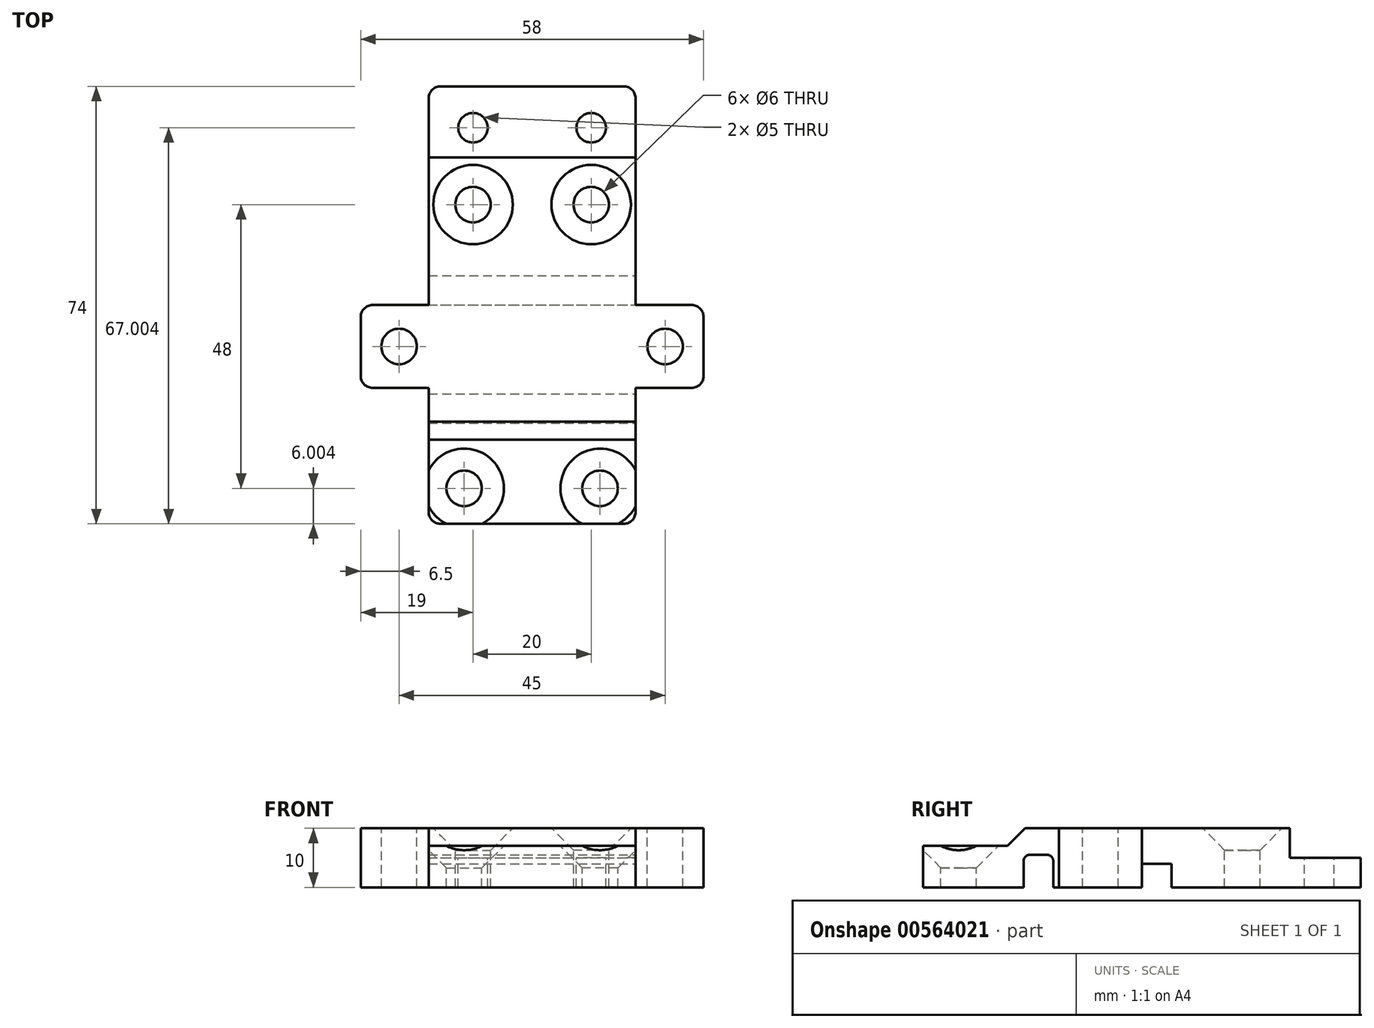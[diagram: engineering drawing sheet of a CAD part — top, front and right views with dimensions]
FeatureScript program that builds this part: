
annotation { "Feature Type Name" : "Feature", "Feature Type Description" : "" }
export const myFeature = defineFeature(function(context is Context, id is Id, definition is map)
    precondition{}
    {
        {
            var Q0;
            Q0=qCreatedBy(makeId("Top.planeOp"),FACE);
            var sketch = newSketch(context, id + "F0", { "sketchPlane" : qUnion([Q0])});
            skLineSegment(sketch, "E0.bottom", {"start": v(0, 48.2) * mm, "end": v(17.5, 48.2) * mm});
            skLineSegment(sketch, "E0.top", {"start": v(0, -25.8) * mm, "end": v(17.5, -25.8) * mm});
            skLineSegment(sketch, "E0.left", {"start": v(0, 48.2) * mm, "end": v(0, -25.8) * mm});
            skLineSegment(sketch, "E0.right", {"start": v(17.5, 48.2) * mm, "end": v(17.5, -25.8) * mm});
            skLineSegment(sketch, "E1.bottom", {"start": v(17.5, -2.8) * mm, "end": v(29, -2.8) * mm});
            skLineSegment(sketch, "E1.top", {"start": v(17.5, 11.2) * mm, "end": v(29, 11.2) * mm});
            skLineSegment(sketch, "E1.left", {"start": v(17.5, -2.8) * mm, "end": v(17.5, 11.2) * mm});
            skLineSegment(sketch, "E1.right", {"start": v(29, -2.8) * mm, "end": v(29, 11.2) * mm});
            skSolve(sketch);
        }
        {
            var Q0;
            Q0=makeQuery(id+"F0.imprint","IMPRINT",FACE,{"disambiguationData":[TD([[makeQuery(id+"F0.imprint","IMPRINT",EDGE,{"derivedFrom":sQuery(id+"F0.wireOp",EDGE,"E1.bottom")}),1.0]])]});
            var Q1;
            {var subQ1=sQuery(id+"F0.wireOp",EDGE,"E0.bottom");Q1=makeQuery(id+"F0.imprint","IMPRINT",FACE,{"disambiguationData":[TD([[makeQuery(id+"F0.imprint","IMPRINT",EDGE,{"derivedFrom":subQ1}),-1.0]])]});}
            extrude(context, id + "F1", {"entities" : qUnion([Q0, Q1]), "depth" : 10 * mm, "offsetDistance" : 25 * mm});
        }
        {
            var Q0;
            {var subQ0=sQuery(id+"F0.wireOp",EDGE,"E0.right");Q0=makeQuery(id+"F1.opExtrude","SWEPT_FACE",FACE,{"disambiguationData":[OSD([subQ0]),TDD([makeQuery(id+"F0.imprint","IMPRINT",EDGE,{"disambiguationData":[TD([[makeQuery(id+"F0.imprint","INTERSECT",VERTEX,{"derivedFrom":[sQuery(id+"F0.wireOp",EDGE,"E0.top"),subQ0]}),1.0]])],"derivedFrom":subQ0})])]});}
            var sketch = newSketch(context, id + "F2", { "sketchPlane" : qUnion([Q0])});
            skLineSegment(sketch, "E2", {"start": v(-25.8, 7) * mm, "end": v(-11.54, 7) * mm});
            skLineSegment(sketch, "E3", {"start": v(-11.54, 7) * mm, "end": v(-8.54, 10) * mm});
            skLineSegment(sketch, "E4", {"start": v(-8.54, 10) * mm, "end": v(-25.8, 10) * mm});
            skLineSegment(sketch, "E5", {"start": v(-25.8, 10) * mm, "end": v(-25.8, 7) * mm});
            skLineSegment(sketch, "E6.bottom", {"start": v(-8.8, 0) * mm, "end": v(-3.8, 0) * mm});
            skLineSegment(sketch, "E6.top", {"start": v(-8.8, 5.5) * mm, "end": v(-3.8, 5.5) * mm});
            skLineSegment(sketch, "E6.left", {"start": v(-8.8, 0) * mm, "end": v(-8.8, 5.5) * mm});
            skLineSegment(sketch, "E6.right", {"start": v(-3.8, 0) * mm, "end": v(-3.8, 5.5) * mm});
            skLineSegment(sketch, "E7", {"start": v(-6.3, 5.5) * mm, "end": v(-6.3, -14.92) * mm, "construction": true});
            skCircle(sketch, "E8", {"center": v(-8.8, 5.5) * mm, "radius": 3 * mm, "construction": true});
            skLineSegment(sketch, "E9.bottom", {"start": v(11.2, 0) * mm, "end": v(16.2, 0) * mm});
            skLineSegment(sketch, "E9.top", {"start": v(11.2, 4) * mm, "end": v(16.2, 4) * mm});
            skLineSegment(sketch, "E9.left", {"start": v(11.2, 0) * mm, "end": v(11.2, 4) * mm});
            skLineSegment(sketch, "E9.right", {"start": v(16.2, 0) * mm, "end": v(16.2, 4) * mm});
            skLineSegment(sketch, "E10.bottom", {"start": v(48.2, 10) * mm, "end": v(36.2, 10) * mm});
            skLineSegment(sketch, "E10.top", {"start": v(48.2, 5) * mm, "end": v(36.2, 5) * mm});
            skLineSegment(sketch, "E10.left", {"start": v(48.2, 10) * mm, "end": v(48.2, 5) * mm});
            skLineSegment(sketch, "E10.right", {"start": v(36.2, 10) * mm, "end": v(36.2, 5) * mm});
            skSolve(sketch);
        }
        {
            var Q0;
            Q0 = qSketchRegion(id + "F2", true);
            extrude(context, id + "F3", {"entities" : qUnion([Q0]), "operationType" : NewBodyOperationType.REMOVE, "endBound" : BoundingType.THROUGH_ALL, "oppositeDirection" : true, "depth" : 25 * mm, "offsetDistance" : 25 * mm});
        }
        {
            var Q0;
            Q0=makeQuery(id+"F3.boolean.opBoolean","COPY",FACE,{"derivedFrom":makeQuery(id+"F3.opExtrude","SWEPT_FACE",FACE,{"disambiguationData":[OSD([sQuery(id+"F2.wireOp",EDGE,"E10.top")])]})});
            var sketch = newSketch(context, id + "F4", { "sketchPlane" : qUnion([Q0])});
            skPoint(sketch, "E11", {"position": v(10, 41.2) * mm});
            skSolve(sketch);
        }
        {
            var Q0;
            Q0=makeQuery(id+"F1.opExtrude","CAP_FACE",FACE,{"disambiguationData":[OSD([sQuery(id+"F0.wireOp",EDGE,"E0.bottom"),sQuery(id+"F0.wireOp",EDGE,"E0.top"),sQuery(id+"F0.wireOp",EDGE,"E0.left"),sQuery(id+"F0.wireOp",EDGE,"E0.right"),sQuery(id+"F0.wireOp",EDGE,"E1.bottom"),sQuery(id+"F0.wireOp",EDGE,"E1.top"),sQuery(id+"F0.wireOp",EDGE,"E1.right")])],"isStart":false});
            var sketch = newSketch(context, id + "F5", { "sketchPlane" : qUnion([Q0])});
            skPoint(sketch, "E12", {"position": v(22.5, 4.2) * mm});
            skLineSegment(sketch, "E13", {"start": v(22.5, 4.2) * mm, "end": v(29, 4.2) * mm, "construction": true});
            skPoint(sketch, "E14", {"position": v(10, 28.2) * mm});
            skSolve(sketch);
        }
        {
            var Q0;
            Q0=makeQuery(id+"F3.boolean.opBoolean","COPY",FACE,{"derivedFrom":makeQuery(id+"F3.opExtrude","SWEPT_FACE",FACE,{"disambiguationData":[OSD([sQuery(id+"F2.wireOp",EDGE,"E2")])]})});
            var sketch = newSketch(context, id + "F6", { "sketchPlane" : qUnion([Q0])});
            skPoint(sketch, "E15", {"position": v(11.5, -19.8) * mm});
            skSolve(sketch);
        }
        {
            var Q0;
            Q0=sQuery(id+"F4.wireOp",VERTEX,"E11");
            var Q1;
            Q1=makeQuery(id+"F1.opExtrude","SWEPT_BODY",BODY,{"disambiguationData":[OSD([sQuery(id+"F0.wireOp",EDGE,"E0.bottom"),sQuery(id+"F0.wireOp",EDGE,"E0.top"),sQuery(id+"F0.wireOp",EDGE,"E0.left"),sQuery(id+"F0.wireOp",EDGE,"E0.right"),sQuery(id+"F0.wireOp",EDGE,"E1.bottom"),sQuery(id+"F0.wireOp",EDGE,"E1.top"),sQuery(id+"F0.wireOp",EDGE,"E1.right")])]});
            hole(context, id + "F7", {"style" : HoleStyle.SIMPLE, "endStyle" : HoleEndStyle.THROUGH, "standardTappedOrClearance" : lookupTablePath({ "standard" : "ISO", "engagement" : "75%", "pitch" : "1 mm", "size" : "M6", "type" : "Tapped" }), "standardBlindInLast" : lookupTablePath({ "standard" : "ISO", "engagement" : "75%", "pitch" : "1 mm", "size" : "M6", "type" : "Tapped" }), "holeDiameter" : 5 * mm, "showTappedDepth" : true, "isTappedThrough" : true, "tappedDepth" : 12 * mm, "tapClearance" : 3, "locations" : qUnion([Q0]), "scope" : qUnion([Q1]), "majorDiameter" : 6 * mm});
        }
        {
            var Q0;
            Q0=sQuery(id+"F5.wireOp",VERTEX,"E12");
            var Q1;
            Q1=makeQuery(id+"F1.opExtrude","SWEPT_BODY",BODY,{"disambiguationData":[OSD([sQuery(id+"F0.wireOp",EDGE,"E0.bottom"),sQuery(id+"F0.wireOp",EDGE,"E0.top"),sQuery(id+"F0.wireOp",EDGE,"E0.left"),sQuery(id+"F0.wireOp",EDGE,"E0.right"),sQuery(id+"F0.wireOp",EDGE,"E1.bottom"),sQuery(id+"F0.wireOp",EDGE,"E1.top"),sQuery(id+"F0.wireOp",EDGE,"E1.right")])]});
            hole(context, id + "F8", {"style" : HoleStyle.SIMPLE, "endStyle" : HoleEndStyle.THROUGH, "standardTappedOrClearance" : lookupTablePath({ "standard" : "ISO", "size" : "6", "type" : "Drilled" }), "standardBlindInLast" : lookupTablePath({ "standard" : "ISO", "size" : "6", "type" : "Drilled" }), "holeDiameter" : 6 * mm, "isTappedThrough" : true, "tappedDepth" : 12 * mm, "tapClearance" : 3, "locations" : qUnion([Q0]), "scope" : qUnion([Q1])});
        }
        {
            var Q0;
            Q0=sQuery(id+"F6.wireOp",VERTEX,"E15");
            var Q1;
            Q1=makeQuery(id+"F1.opExtrude","SWEPT_BODY",BODY,{"disambiguationData":[OSD([sQuery(id+"F0.wireOp",EDGE,"E0.bottom"),sQuery(id+"F0.wireOp",EDGE,"E0.top"),sQuery(id+"F0.wireOp",EDGE,"E0.left"),sQuery(id+"F0.wireOp",EDGE,"E0.right"),sQuery(id+"F0.wireOp",EDGE,"E1.bottom"),sQuery(id+"F0.wireOp",EDGE,"E1.top"),sQuery(id+"F0.wireOp",EDGE,"E1.right")])]});
            hole(context, id + "F9", {"style" : HoleStyle.C_SINK, "endStyle" : HoleEndStyle.THROUGH, "standardTappedOrClearance" : lookupTablePath({ "standard" : "ISO", "size" : "6", "type" : "Drilled" }), "standardBlindInLast" : lookupTablePath({ "standard" : "ISO", "size" : "6", "type" : "Drilled" }), "holeDiameter" : 6 * mm, "cSinkDiameter" : 13.44 * mm, "cSinkAngle" : 90 * degree, "isTappedThrough" : true, "tappedDepth" : 12 * mm, "tapClearance" : 3, "startFromSketch" : true, "locations" : qUnion([Q0]), "scope" : qUnion([Q1])});
        }
        {
            var Q0;
            Q0=makeQuery(id+"F1.opExtrude","CAP_FACE",FACE,{"disambiguationData":[OSD([sQuery(id+"F0.wireOp",EDGE,"E0.bottom"),sQuery(id+"F0.wireOp",EDGE,"E0.top"),sQuery(id+"F0.wireOp",EDGE,"E0.left"),sQuery(id+"F0.wireOp",EDGE,"E0.right"),sQuery(id+"F0.wireOp",EDGE,"E1.bottom"),sQuery(id+"F0.wireOp",EDGE,"E1.top"),sQuery(id+"F0.wireOp",EDGE,"E1.right")])],"isStart":false});
            var sketch = newSketch(context, id + "F10", { "sketchPlane" : qUnion([Q0])});
            skPoint(sketch, "E16", {"position": v(10, 28.2) * mm});
            skSolve(sketch);
        }
        {
            var Q0;
            Q0=sQuery(id+"F10.wireOp",VERTEX,"E16");
            var Q1;
            Q1=makeQuery(id+"F1.opExtrude","SWEPT_BODY",BODY,{"disambiguationData":[OSD([sQuery(id+"F0.wireOp",EDGE,"E0.bottom"),sQuery(id+"F0.wireOp",EDGE,"E0.top"),sQuery(id+"F0.wireOp",EDGE,"E0.left"),sQuery(id+"F0.wireOp",EDGE,"E0.right"),sQuery(id+"F0.wireOp",EDGE,"E1.bottom"),sQuery(id+"F0.wireOp",EDGE,"E1.top"),sQuery(id+"F0.wireOp",EDGE,"E1.right")])]});
            hole(context, id + "F11", {"style" : HoleStyle.C_SINK, "endStyle" : HoleEndStyle.THROUGH, "standardTappedOrClearance" : lookupTablePath({ "standard" : "ISO", "size" : "6", "type" : "Drilled" }), "standardBlindInLast" : lookupTablePath({ "standard" : "ISO", "size" : "6", "type" : "Drilled" }), "holeDiameter" : 6 * mm, "cSinkDiameter" : 13.44 * mm, "cSinkAngle" : 90 * degree, "isTappedThrough" : true, "tappedDepth" : 12 * mm, "tapClearance" : 3, "locations" : qUnion([Q0]), "scope" : qUnion([Q1])});
        }
        {
            var Q0;
            Q0=makeQuery(id+"F1.opExtrude","SWEPT_EDGE",EDGE,{"disambiguationData":[OSD([sQuery(id+"F0.wireOp",EDGE,"E1.bottom"),sQuery(id+"F0.wireOp",EDGE,"E1.right")])]});
            var Q1;
            Q1=makeQuery(id+"F1.opExtrude","SWEPT_EDGE",EDGE,{"disambiguationData":[OSD([sQuery(id+"F0.wireOp",EDGE,"E1.top"),sQuery(id+"F0.wireOp",EDGE,"E1.right")])]});
            var Q2;
            Q2=makeQuery(id+"F1.opExtrude","SWEPT_EDGE",EDGE,{"disambiguationData":[OSD([sQuery(id+"F0.wireOp",EDGE,"E0.bottom"),sQuery(id+"F0.wireOp",EDGE,"E0.right")])]});
            var Q3;
            Q3=makeQuery(id+"F1.opExtrude","SWEPT_EDGE",EDGE,{"disambiguationData":[OSD([sQuery(id+"F0.wireOp",EDGE,"E0.top"),sQuery(id+"F0.wireOp",EDGE,"E0.right")])]});
            fillet(context, id + "F12", {"entities" : qUnion([Q0, Q1, Q2, Q3]), "radius" : 2 * mm, "tangentPropagation" : true, "allowEdgeOverflow" : false});
        }
        {
            var Q0;
            Q0=makeQuery(id+"F3.boolean.opBoolean","COPY",EDGE,{"derivedFrom":makeQuery(id+"F3.opExtrude","CAP_EDGE",EDGE,{"disambiguationData":[OSD([sQuery(id+"F2.wireOp",EDGE,"E6.top")])],"isStart":true})});
            var Q1;
            Q1=makeQuery(id+"F3.boolean.opBoolean","COPY",EDGE,{"derivedFrom":makeQuery(id+"F3.opExtrude","SWEPT_EDGE",EDGE,{"disambiguationData":[OSD([sQuery(id+"F2.wireOp",EDGE,"E6.top"),sQuery(id+"F2.wireOp",EDGE,"E6.right")])]})});
            var Q2;
            Q2=makeQuery(id+"F3.boolean.opBoolean","COPY",EDGE,{"derivedFrom":makeQuery(id+"F3.opExtrude","SWEPT_EDGE",EDGE,{"disambiguationData":[OSD([sQuery(id+"F2.wireOp",EDGE,"E6.top"),sQuery(id+"F2.wireOp",EDGE,"E6.left")])]})});
            fillet(context, id + "F13", {"entities" : qUnion([Q0, Q1, Q2]), "radius" : 1 * mm, "tangentPropagation" : true, "allowEdgeOverflow" : false});
        }
        {
            var Q0;
            Q0=makeQuery(id+"F1.opExtrude","SWEPT_BODY",BODY,{"disambiguationData":[OSD([sQuery(id+"F0.wireOp",EDGE,"E0.bottom"),sQuery(id+"F0.wireOp",EDGE,"E0.top"),sQuery(id+"F0.wireOp",EDGE,"E0.left"),sQuery(id+"F0.wireOp",EDGE,"E0.right"),sQuery(id+"F0.wireOp",EDGE,"E1.bottom"),sQuery(id+"F0.wireOp",EDGE,"E1.top"),sQuery(id+"F0.wireOp",EDGE,"E1.right")])]});
            var Q1;
            Q1=makeQuery(id+"F1.opExtrude","SWEPT_FACE",FACE,{"disambiguationData":[OSD([sQuery(id+"F0.wireOp",EDGE,"E0.left")])]});
            mirror(context, id + "F14", {"operationType" : NewBodyOperationType.ADD, "entities" : qUnion([Q0]), "mirrorPlane" : qUnion([Q1])});
        }
    });
